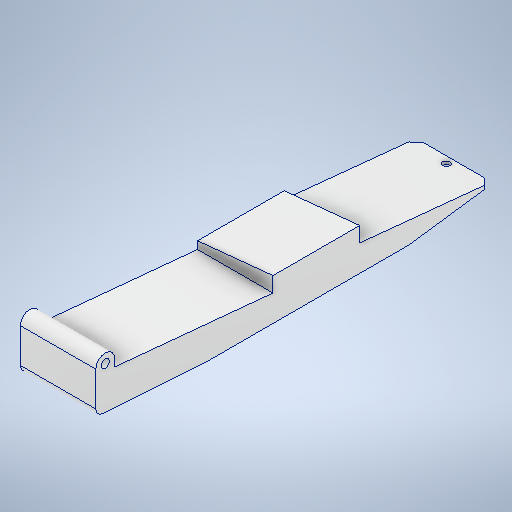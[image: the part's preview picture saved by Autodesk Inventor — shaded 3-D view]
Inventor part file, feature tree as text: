
AUTODESK INVENTOR PART (.ipt)
format: ipt  version: 2025 (Build 290162010, 162A)  size: 327,680 bytes
history: native  units: mm
features: chamfer x6, sketch x5, hole x3, extrude x2, fillet x2, plane x1, other x1
ambient origin geometry x8: Origin, YZ Plane, XZ Plane, XY Plane, X Axis, Y Axis, Z Axis, Center Point
bodies: Volumenkörper1 (feature_tree)
feature tree (20):
  extrude  "Extrusion1"  Depth=20.0mm
  extrude  "Extrusion3"  Depth=5.0mm
  fillet  "Rundung2"  Radius=8.5mm
  hole  "Bohrung1"  [1 undecoded]
  chamfer  "Fasen2"  Distance=42.0mm Angle=45.0deg
  chamfer  "Fasen3"  Distance=35.0mm Angle=45.0deg
  plane  "Arbeitsebene1"
  hole  "Bohrung3"  [1 undecoded]
  chamfer  "Fasen5"  Distance=3.0mm Angle=45.0deg
  hole  "Bohrung4"  [1 undecoded]
  chamfer  "Fasen6"  Distance=20.0mm Angle=45.0deg
  other  "Verdickung1"
  chamfer  "Fasen7"  Distance=2.0mm Angle=45.0deg
  chamfer  "Fasen8"  Distance=2.0mm
  fillet  "Rundung4"  [1 undecoded]
  sketch  "Skizze1"  dims[d0=7.0mm d1=0.0mm d2=20.0mm]
  sketch  "Skizze3"  dims[d3=105.0mm d8=5.0mm d9=8.5mm d10=0.0mm]
  sketch  "Skizze4"  dims[d11=2.5mm]
  sketch  "Skizze7"  dims[d13=2.2mm d14=6.0mm d15=4.0mm d16=2.0mm d17=90.0deg d18=5.0mm d19=20.594885mm d34=2.0mm d35=2.0mm d36=45.0deg d37=4.0mm d38=42.0mm d39=45.0deg]
  sketch  "Skizze8"  dims[d40=2.2mm d41=6.0mm d42=4.0mm d43=2.0mm d44=90.0deg d45=5.0mm d46=20.594885mm d50=35.0mm d51=3.5mm d52=45.0deg d53=2.0mm d54=2.0mm d55=5.0mm d56=4.0mm d57=2.0mm d58=90.0deg d59=6.3mm d60=20.594885mm d61=3.0mm d62=22.0mm d63=45.0deg d64=4.0mm d65=1.0mm d66=20.0mm d67=2.0mm d68=45.0deg d69=30.0mm d70=2.0mm d71=45.0deg d72=2.0mm]
note: 4 required parameter values undecoded (feature->parameter linkage not recoverable at this tier; creation-order binding heuristic only, values carry confidence <= 0.55)
